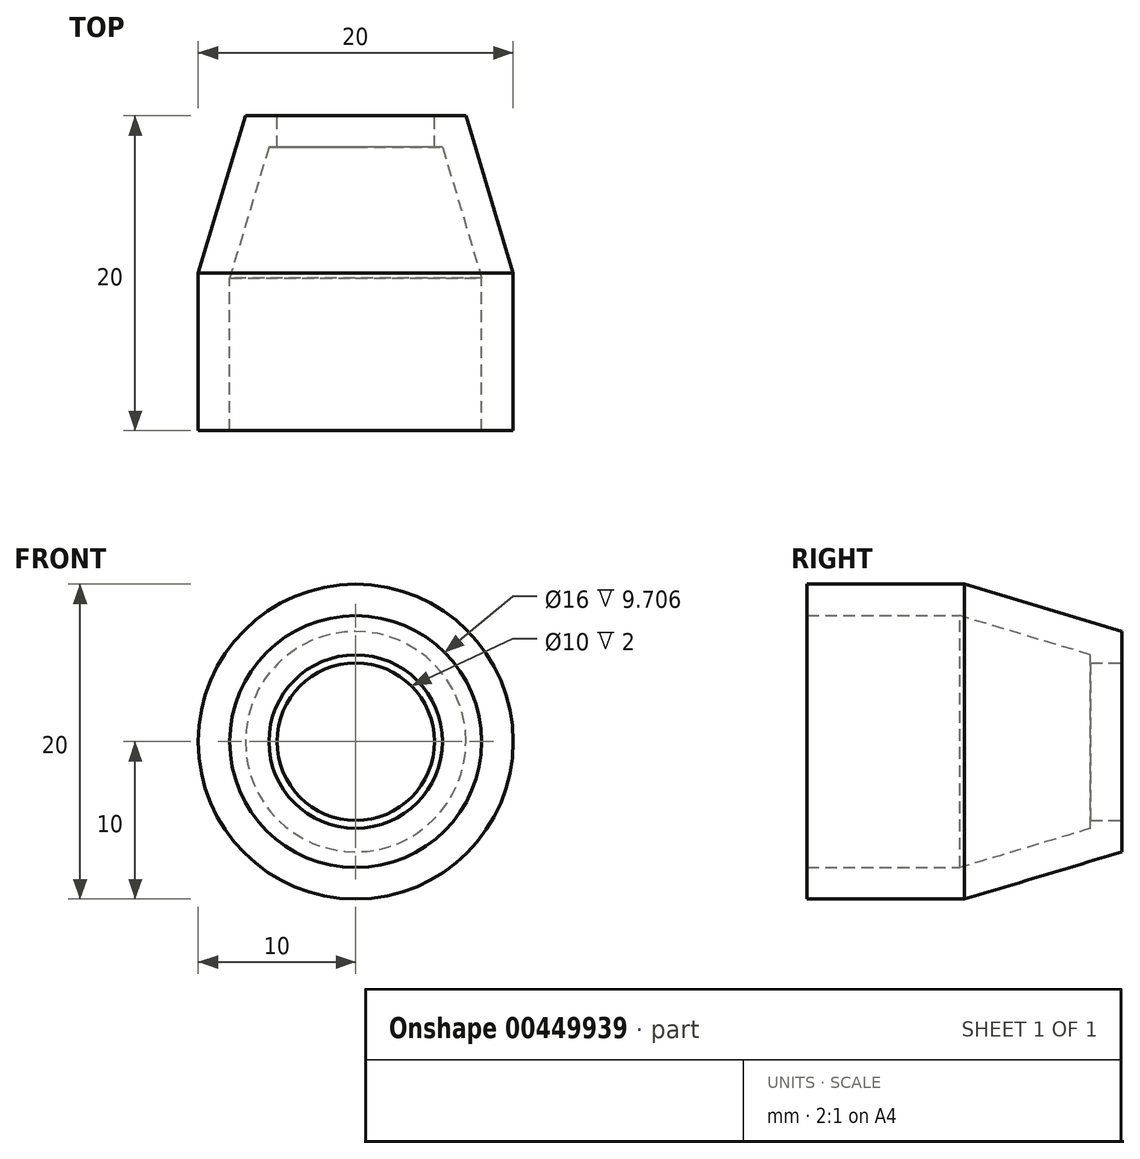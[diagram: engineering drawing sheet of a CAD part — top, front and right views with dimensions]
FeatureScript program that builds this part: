
annotation { "Feature Type Name" : "Feature", "Feature Type Description" : "" }
export const myFeature = defineFeature(function(context is Context, id is Id, definition is map)
    precondition{}
    {
        {
            var Q0;
            Q0=qCreatedBy(makeId("Front.planeOp"),FACE);
            var sketch = newSketch(context, id + "F0", { "sketchPlane" : qUnion([Q0])});
            skCircle(sketch, "E0", {"center": v(0, 0) * mm, "radius": 10 * mm});
            skSolve(sketch);
        }
        {
            var Q0;
            Q0=makeQuery(id+"F0.imprint","IMPRINT",FACE,{"disambiguationData":[TD([[makeQuery(id+"F0.imprint","IMPRINT",EDGE,{"derivedFrom":sQuery(id+"F0.wireOp",EDGE,"E0")}),1.0]])]});
            extrude(context, id + "F1", {"entities" : qUnion([Q0]), "depth" : 10 * mm});
        }
        {
            var Q0;
            Q0=makeQuery(id+"F1.opExtrude","CAP_FACE",FACE,{"disambiguationData":[OSD([sQuery(id+"F0.wireOp",EDGE,"E0")])],"isStart":true});
            var sketch = newSketch(context, id + "F2", { "sketchPlane" : qUnion([Q0])});
            skCircle(sketch, "E1", {"center": v(0, 0) * mm, "radius": 7 * mm});
            skSolve(sketch);
        }
        {
            var Q1;
            Q1=makeQuery(id+"F1.opExtrude","CAP_FACE",FACE,{"disambiguationData":[OSD([sQuery(id+"F0.wireOp",EDGE,"E0")])],"isStart":false});
            var Q2;
            Q2 = qSketchRegion(id + "F2", true);
            loft(context, id + "F3", {"operationType" : NewBodyOperationType.INTERSECT, "sheetProfilesArray" : [{ "sheetProfileEntities" : qUnion([Q1]) }, { "sheetProfileEntities" : qUnion([Q2]) }]});
        }
        {
            var Q0;
            Q0=makeQuery(id+"F1.opExtrude","CAP_FACE",FACE,{"disambiguationData":[OSD([sQuery(id+"F0.wireOp",EDGE,"E0")])],"isStart":false});
            extrude(context, id + "F4", {"entities" : qUnion([Q0]), "operationType" : NewBodyOperationType.ADD, "depth" : 10 * mm});
        }
        {
            var Q0;
            Q0=makeQuery(id+"F4.opExtrude","CAP_FACE",FACE,{"disambiguationData":[OSD([sQuery(id+"F0.wireOp",EDGE,"E0")])],"isStart":false});
            shell(context, id + "F5", {"entities" : qUnion([Q0]), "thickness" : 2 * mm});
        }
        {
            var Q0;
            Q0=makeQuery(id+"F1.opExtrude","CAP_FACE",FACE,{"disambiguationData":[OSD([sQuery(id+"F0.wireOp",EDGE,"E0")])],"isStart":true});
            var sketch = newSketch(context, id + "F6", { "sketchPlane" : qUnion([Q0])});
            skCircle(sketch, "E2", {"center": v(0, 0) * mm, "radius": 5 * mm});
            skSolve(sketch);
        }
        {
            var Q0;
            Q0=makeQuery(id+"F6.imprint","IMPRINT",FACE,{"disambiguationData":[TD([[makeQuery(id+"F6.imprint","IMPRINT",EDGE,{"derivedFrom":sQuery(id+"F6.wireOp",EDGE,"E2")}),1.0]])]});
            extrude(context, id + "F7", {"entities" : qUnion([Q0]), "operationType" : NewBodyOperationType.REMOVE, "oppositeDirection" : true, "depth" : 2 * mm});
        }
    });
